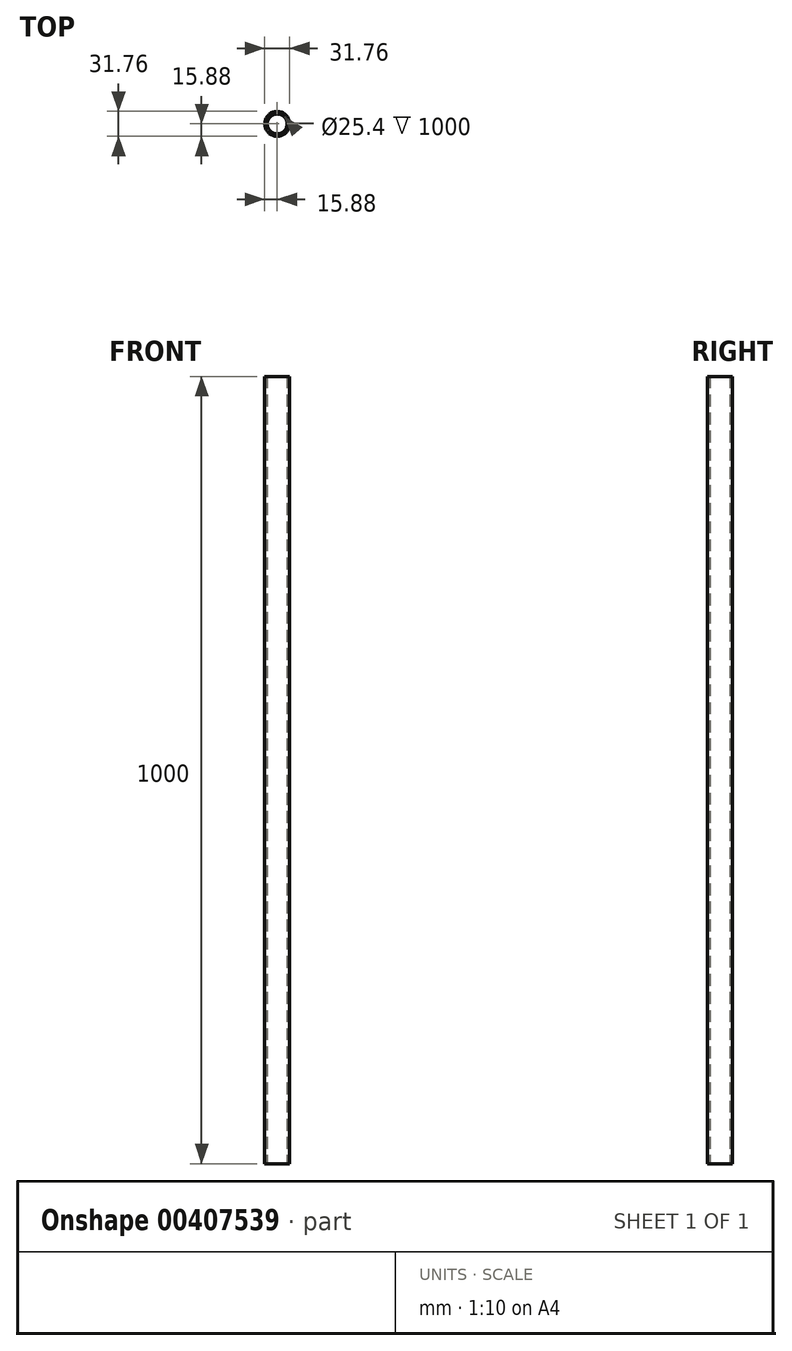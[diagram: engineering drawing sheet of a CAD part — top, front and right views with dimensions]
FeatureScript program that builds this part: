
annotation { "Feature Type Name" : "Feature", "Feature Type Description" : "" }
export const myFeature = defineFeature(function(context is Context, id is Id, definition is map)
    precondition{}
    {
        {
            var Q0;
            Q0=qCreatedBy(makeId("Top.planeOp"),FACE);
            var sketch = newSketch(context, id + "F0", { "sketchPlane" : qUnion([Q0])});
            skCircle(sketch, "E0", {"center": v(0, 0) * mm, "radius": 15.88 * mm});
            skCircle(sketch, "E1", {"center": v(0, 0) * mm, "radius": 12.7 * mm});
            skSolve(sketch);
        }
        {
            var Q0;
            Q0 = qSketchRegion(id + "F0", true);
            extrude(context, id + "F1", {"entities" : qUnion([Q0]), "depth" : 1000 * mm, "offsetDistance" : 25 * mm});
        }
    });
